# Revit family: S-tank_Solar_DUO_SS
name_source: partatom
category: Оборудование
units: mm (PartAtom-declared; Revit-internal decimal feet)

## family parameters
Всегда вертикально = Да
Классификация = Нет
На основе рабочей плоскости = Нет
Общий = Нет
При загрузке вырезать с полостями = Нет
Размер круглого соединителя = Использовать диаметр
Тип детали = Нормальный
Точка расчета площади = Нет

## types (9) — shared parameters
ADSK_URL документации изделия = http://s-tank.ru
ADSK_Группирование = Оборудование
ADSK_Единица измерения = шт.
ADSK_Завод-изготовитель = ООО “С-ТЭНК ВОТЕР ХИТЕРС”
ADSK_Наименование = Бойлер косвенного нагрева
DN1 = 25 мм
DN2 = 15 мм
shrf = 18 мм
Разработка семейств = https://rubim.tech

## per-type parameters (varying)
| type | A | ADSK_Код изделия | ADSK_Марка | ADSK_Масса | ADSK_Обозначение | B | C | D | E | H | I | J | K | L | a | Диаметрcизоляцией |
| SS Solarduo 200 | 210 мм | 2.1002 | SS Solar duo 200 | 64 | SSSolarduo 200 | 320 мм | 395 мм | 520 мм | 630 мм | 1220 мм | 740 мм | 1030 мм | 895 мм | 970 мм | 105 мм | 630 мм |
| SS Solarduo 300 | 210 мм | 2.1003 | SS Solar duo 300 | 73 | SSSolarduo 300 | 330 мм | 410 мм | 620 мм | 740 мм | 1220 мм | 860 мм | 1030 мм | 1090 мм | 1170 мм | 105 мм | 630 мм |
| SS Solarduo 500 | 205 мм | 2.1004 | SS Solar duo 500 | 97 | SSSolarduo 500 | 335 мм | 415 мм | 585 мм | 715 мм | 1605 мм | 845 мм | 1365 мм | 995 мм | 1075 мм | 130 мм | 780 мм |
| SS Solarduo 750 | 195 мм | 2.1005 | SS Solar duo 750 | 119 | SSSolarduo 750 | 325 мм | 405 мм | 515 мм | 645 мм | 1630 мм | 775 мм | 1585 мм | 925 мм | 1005 мм | 153 мм | 920 мм |
| SS Solarduo 1000 | 205 мм | 2.1006 | SS Solar duo 1000 | 153 | SSSolarduo 1000 | 395 мм | 490 мм | 605 мм | 795 мм | 2205 мм | 985 мм | 1920 мм | 1120 мм | 1215 мм | 153 мм | 920 мм |
| SS Solarduo 1200 | 285 мм | 2.1007 | SS Solar duo 1200 | 195 | SSSolarduo 1200 | 445 мм | 520 мм | 645 мм | 805 мм | 2020 мм | 965 мм | 1655 мм | 1160 мм | 1235 мм | 158 мм | 950 мм |
| SS Solarduo 1500 | 275 мм | 2.1008 | SS Solar duo 1500 | 225 | SSSolarduo 1500 | 465 мм | 560 мм | 745 мм | 935 мм | 2370 мм | 1125 мм | 2005 мм | 1500 мм | 1595 мм | 158 мм | 950 мм |
| SS Solarduo 2000 | 370 мм | 2.1009 | SS Solar duo 2000 | 270 | SSSolarduo 2000 | 530 мм | 605 мм | 890 мм | 1050 мм | 2100 мм | 1210 мм | 1740 мм | 1505 мм | 1580 мм | 225 мм | 1350 мм |
| SS Solarduo 3000 | 403 мм | 2.1010 | SS Solar duo 3000 | 0 | SSSolarduo 3000 | 563 мм | 638 мм | 903 мм | 1063 мм | 2210 мм | 1223 мм | 1773 мм | 1548 мм | 1623 мм | 290 мм | 1740 мм |
